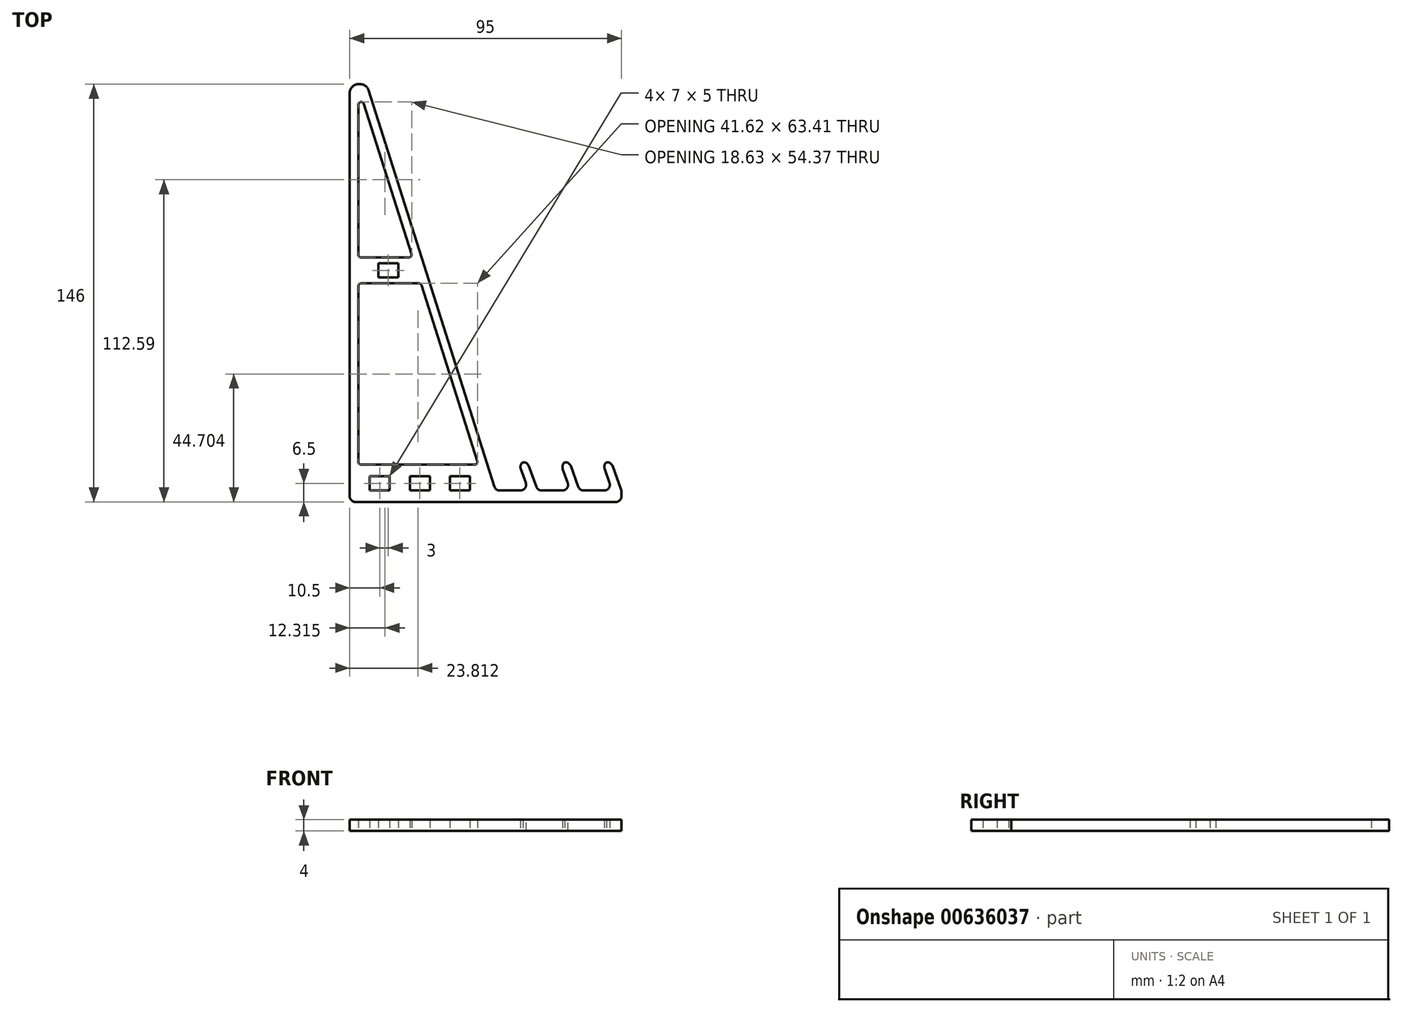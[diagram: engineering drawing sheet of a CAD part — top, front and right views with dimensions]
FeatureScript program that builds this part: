
annotation { "Feature Type Name" : "Feature", "Feature Type Description" : "" }
export const myFeature = defineFeature(function(context is Context, id is Id, definition is map)
    precondition{}
    {
        {
            var Q0;
            Q0=qCreatedBy(makeId("Top.planeOp"),FACE);
            var sketch = newSketch(context, id + "F0", { "sketchPlane" : qUnion([Q0])});
            skLineSegment(sketch, "E0", {"start": v(44, -4) * mm, "end": v(-51, -4) * mm});
            skLineSegment(sketch, "E1", {"start": v(-51, -4) * mm, "end": v(-51, 139) * mm});
            skLineSegment(sketch, "E2.bottom", {"start": v(-44, 5) * mm, "end": v(-37, 5) * mm});
            skLineSegment(sketch, "E2.top", {"start": v(-44, 0) * mm, "end": v(-37, 0) * mm});
            skLineSegment(sketch, "E2.left", {"start": v(-44, 5) * mm, "end": v(-44, 0) * mm});
            skLineSegment(sketch, "E2.right", {"start": v(-37, 5) * mm, "end": v(-37, 0) * mm});
            skLineSegment(sketch, "E3", {"start": v(-44.43, 139.9) * mm, "end": v(0, 0) * mm});
            skLineSegment(sketch, "E4", {"start": v(-46.05, 135.09) * mm, "end": v(-29.41, 82.71) * mm});
            skLineSegment(sketch, "E5", {"start": v(-30.37, 81.4) * mm, "end": v(-47, 81.4) * mm});
            skLineSegment(sketch, "E6", {"start": v(-48, 82.4) * mm, "end": v(-48, 134.78) * mm});
            skLineSegment(sketch, "E7", {"start": v(-47, 9) * mm, "end": v(-7.37, 9) * mm});
            skLineSegment(sketch, "E8", {"start": v(-6.42, 10.3) * mm, "end": v(-25.92, 71.71) * mm});
            skLineSegment(sketch, "E9", {"start": v(-26.87, 72.4) * mm, "end": v(-47, 72.4) * mm});
            skLineSegment(sketch, "E10", {"start": v(-48, 71.4) * mm, "end": v(-48, 10) * mm});
            skPoint(sketch, "E11.visualSharp", {"position": v(-48, 141.24) * mm});
            skArc(sketch, "E11.filletArc", {"start": v(-46.05, 135.09) * mm, "mid": v(-47.15, 135.77) * mm, "end": v(-48, 134.78) * mm});
            skPoint(sketch, "E12.visualSharp", {"position": v(-48, 81.4) * mm});
            skArc(sketch, "E12.filletArc", {"start": v(-48, 82.4) * mm, "mid": v(-47.7, 81.7) * mm, "end": v(-47, 81.4) * mm});
            skPoint(sketch, "E13.visualSharp", {"position": v(-29, 81.4) * mm});
            skArc(sketch, "E13.filletArc", {"start": v(-30.37, 81.4) * mm, "mid": v(-29.56, 81.82) * mm, "end": v(-29.41, 82.71) * mm});
            skPoint(sketch, "E14.visualSharp", {"position": v(-26.14, 72.4) * mm});
            skArc(sketch, "E14.filletArc", {"start": v(-25.92, 71.71) * mm, "mid": v(-26.28, 72.21) * mm, "end": v(-26.87, 72.4) * mm});
            skPoint(sketch, "E15.visualSharp", {"position": v(-48, 72.4) * mm});
            skArc(sketch, "E15.filletArc", {"start": v(-47, 72.4) * mm, "mid": v(-47.7, 72.11) * mm, "end": v(-48, 71.4) * mm});
            skPoint(sketch, "E16.visualSharp", {"position": v(-48, 9) * mm});
            skArc(sketch, "E16.filletArc", {"start": v(-48, 10) * mm, "mid": v(-47.7, 9.3) * mm, "end": v(-47, 9) * mm});
            skPoint(sketch, "E17.visualSharp", {"position": v(-6, 9) * mm});
            skArc(sketch, "E17.filletArc", {"start": v(-7.37, 9) * mm, "mid": v(-6.57, 9.4) * mm, "end": v(-6.42, 10.3) * mm});
            skLineSegment(sketch, "E18.1.0.0", {"start": v(-30, 5) * mm, "end": v(-23, 5) * mm});
            skLineSegment(sketch, "E18.1.0.1", {"start": v(-23, 5) * mm, "end": v(-23, 0) * mm});
            skLineSegment(sketch, "E18.1.0.2", {"start": v(-30, 0) * mm, "end": v(-23, 0) * mm});
            skLineSegment(sketch, "E18.1.0.3", {"start": v(-30, 5) * mm, "end": v(-30, 0) * mm});
            skLineSegment(sketch, "E18.2.0.0", {"start": v(-16, 5) * mm, "end": v(-9, 5) * mm});
            skLineSegment(sketch, "E18.2.0.1", {"start": v(-9, 5) * mm, "end": v(-9, 0) * mm});
            skLineSegment(sketch, "E18.2.0.2", {"start": v(-16, 0) * mm, "end": v(-9, 0) * mm});
            skLineSegment(sketch, "E18.2.0.3", {"start": v(-16, 5) * mm, "end": v(-16, 0) * mm});
            skLineSegment(sketch, "E18.direction1", {"start": v(-44, 5) * mm, "end": v(-30, 5) * mm, "construction": true});
            skLineSegment(sketch, "E19.bottom", {"start": v(-41, 79.4) * mm, "end": v(-34, 79.4) * mm});
            skLineSegment(sketch, "E19.top", {"start": v(-41, 74.4) * mm, "end": v(-34, 74.4) * mm});
            skLineSegment(sketch, "E19.left", {"start": v(-41, 79.4) * mm, "end": v(-41, 74.4) * mm});
            skLineSegment(sketch, "E19.right", {"start": v(-34, 79.4) * mm, "end": v(-34, 74.4) * mm});
            skLineSegment(sketch, "E20", {"start": v(-48, 142) * mm, "end": v(-47.29, 142) * mm});
            skPoint(sketch, "E21.visualSharp", {"position": v(-45.1, 142) * mm});
            skArc(sketch, "E21.filletArc", {"start": v(-44.43, 139.9) * mm, "mid": v(-45.52, 141.42) * mm, "end": v(-47.29, 142) * mm});
            skPoint(sketch, "E22.visualSharp", {"position": v(-51, 142) * mm});
            skArc(sketch, "E22.filletArc", {"start": v(-48, 142) * mm, "mid": v(-50.12, 141.12) * mm, "end": v(-51, 139) * mm});
            skLineSegment(sketch, "E23", {"start": v(11.5, 0) * mm, "end": v(8.08, 9.4) * mm});
            skLineSegment(sketch, "E24", {"start": v(8.08, 9.4) * mm, "end": v(10.9, 10.42) * mm});
            skLineSegment(sketch, "E25", {"start": v(10.9, 10.42) * mm, "end": v(14.7, 0) * mm});
            skLineSegment(sketch, "E26", {"start": v(0, 0) * mm, "end": v(44, 0) * mm});
            skLineSegment(sketch, "E27", {"start": v(44, 0) * mm, "end": v(44, -4) * mm});
            skLineSegment(sketch, "E28", {"start": v(44, 0) * mm, "end": v(40.2, 10.42) * mm});
            skLineSegment(sketch, "E29", {"start": v(40.2, 10.42) * mm, "end": v(37.39, 9.4) * mm});
            skLineSegment(sketch, "E30", {"start": v(37.39, 9.4) * mm, "end": v(40.8, 0) * mm});
            skLineSegment(sketch, "E31", {"start": v(40.8, 0) * mm, "end": v(44, 0) * mm});
            skLineSegment(sketch, "E32", {"start": v(26.2, 0) * mm, "end": v(22.77, 9.4) * mm});
            skLineSegment(sketch, "E33", {"start": v(22.77, 9.4) * mm, "end": v(25.6, 10.42) * mm});
            skLineSegment(sketch, "E34", {"start": v(25.6, 10.42) * mm, "end": v(29.39, 0) * mm});
            skLineSegment(sketch, "E35", {"start": v(29.39, 0) * mm, "end": v(26.2, 0) * mm});
            skSolve(sketch);
        }
        {
            var Q0;
            Q0=qSketchRegion(id+"F0",true);
            extrude(context, id + "F1", {"entities" : qUnion([Q0]), "depth" : 4 * mm, "offsetDistance" : 25 * mm});
        }
        {
            var Q0;
            Q0=makeQuery(id+"F1.opExtrude","SWEPT_EDGE",EDGE,{"disambiguationData":[OSD([sQuery(id+"F0.wireOp",EDGE,"E0"),sQuery(id+"F0.wireOp",EDGE,"E1")])]});
            var Q1;
            Q1=makeQuery(id+"F1.opExtrude","SWEPT_EDGE",EDGE,{"disambiguationData":[OSD([sQuery(id+"F0.wireOp",EDGE,"E0"),sQuery(id+"F0.wireOp",EDGE,"E27")])]});
            var Q2;
            Q2=makeQuery(id+"F1.opExtrude","SWEPT_EDGE",EDGE,{"disambiguationData":[OSD([sQuery(id+"F0.wireOp",EDGE,"E27"),sQuery(id+"F0.wireOp",EDGE,"E28"),sQuery(id+"F0.wireOp",EDGE,"E31")])]});
            var Q3;
            Q3=makeQuery(id+"F1.opExtrude","SWEPT_EDGE",EDGE,{"disambiguationData":[OSD([sQuery(id+"F0.wireOp",EDGE,"E28"),sQuery(id+"F0.wireOp",EDGE,"E29")])]});
            var Q4;
            Q4=makeQuery(id+"F1.opExtrude","SWEPT_EDGE",EDGE,{"disambiguationData":[OSD([sQuery(id+"F0.wireOp",EDGE,"E29"),sQuery(id+"F0.wireOp",EDGE,"E30")])]});
            var Q5;
            Q5=makeQuery(id+"F1.opExtrude","SWEPT_EDGE",EDGE,{"disambiguationData":[OSD([sQuery(id+"F0.wireOp",EDGE,"E26"),sQuery(id+"F0.wireOp",EDGE,"E30"),sQuery(id+"F0.wireOp",EDGE,"E31")])]});
            var Q6;
            Q6=makeQuery(id+"F1.opExtrude","SWEPT_EDGE",EDGE,{"disambiguationData":[OSD([sQuery(id+"F0.wireOp",EDGE,"E25"),sQuery(id+"F0.wireOp",EDGE,"E26")])]});
            var Q7;
            Q7=makeQuery(id+"F1.opExtrude","SWEPT_EDGE",EDGE,{"disambiguationData":[OSD([sQuery(id+"F0.wireOp",EDGE,"E24"),sQuery(id+"F0.wireOp",EDGE,"E25")])]});
            var Q8;
            Q8=makeQuery(id+"F1.opExtrude","SWEPT_EDGE",EDGE,{"disambiguationData":[OSD([sQuery(id+"F0.wireOp",EDGE,"E23"),sQuery(id+"F0.wireOp",EDGE,"E24")])]});
            var Q9;
            Q9=makeQuery(id+"F1.opExtrude","SWEPT_EDGE",EDGE,{"disambiguationData":[OSD([sQuery(id+"F0.wireOp",EDGE,"E23"),sQuery(id+"F0.wireOp",EDGE,"E26")])]});
            var Q10;
            Q10=makeQuery(id+"F1.opExtrude","SWEPT_EDGE",EDGE,{"disambiguationData":[OSD([sQuery(id+"F0.wireOp",EDGE,"E3"),sQuery(id+"F0.wireOp",EDGE,"E26")])]});
            var Q11;
            Q11=makeQuery(id+"F1.opExtrude","SWEPT_EDGE",EDGE,{"disambiguationData":[OSD([sQuery(id+"F0.wireOp",EDGE,"E32"),sQuery(id+"F0.wireOp",EDGE,"E33")])]});
            var Q12;
            Q12=makeQuery(id+"F1.opExtrude","SWEPT_EDGE",EDGE,{"disambiguationData":[OSD([sQuery(id+"F0.wireOp",EDGE,"E33"),sQuery(id+"F0.wireOp",EDGE,"E34")])]});
            var Q13;
            Q13=makeQuery(id+"F1.opExtrude","SWEPT_EDGE",EDGE,{"disambiguationData":[OSD([sQuery(id+"F0.wireOp",EDGE,"E26"),sQuery(id+"F0.wireOp",EDGE,"E32"),sQuery(id+"F0.wireOp",EDGE,"E35")])]});
            var Q14;
            Q14=makeQuery(id+"F1.opExtrude","SWEPT_EDGE",EDGE,{"disambiguationData":[OSD([sQuery(id+"F0.wireOp",EDGE,"E26"),sQuery(id+"F0.wireOp",EDGE,"E34"),sQuery(id+"F0.wireOp",EDGE,"E35")])]});
            fillet(context, id + "F2", {"entities" : qUnion([Q0, Q1, Q2, Q3, Q4, Q5, Q6, Q7, Q8, Q9, Q10, Q11, Q12, Q13, Q14]), "radius" : 2 * mm, "tangentPropagation" : true, "allowEdgeOverflow" : false});
        }
    });
